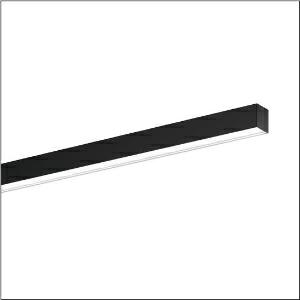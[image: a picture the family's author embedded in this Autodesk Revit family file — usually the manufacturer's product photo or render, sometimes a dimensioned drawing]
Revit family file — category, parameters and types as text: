
# Revit family: silica_r__21_51mx23tbt5b_7df7
name_source: partatom
category: Lighting Fixtures
units: mm (PartAtom-declared; Revit-internal decimal feet)

## family parameters
Cut with Voids When Loaded = No
Host = Face
Light Source = No
Part Type = Normal
Room Calculation Point = No
Round Connector Dimension = Use Diameter
Shared = No

## types (1)
- --- (1 x LED, 4030 lm, 40.5 W, 6500K)
    Apparent Load = 41 VA
    CIE Flux Codes = 78 96 99 100 100
    Color Rendering = 80
    Color Temperature = 6500K
    Default Elevation = 1800 mm
    Description = Silica® 21, office luminaire, primary optical cover: prismatic diffuser, of PMMA, CAT 2 (L<= 3000cd/m²), light emission: direct distribution, primary light characteristic: symmetric, installation type: surface-mounted, LED, rated luminous flux: 4.030lm, luminous efficacy: 95lm/W, light colour: 8tw, colour temperature: 2700..6500K, control gear: ECG DALI, with terminal, 3+2-pole, max. 2.5mm², mains connection: 220..240V, AC, 50/60Hz, rated input power: 42.6W, luminaire housing, of aluminium, jet black (RAL 9005), length: 1.504mm, width: 53mm, height: 53mm, protection rating (complete): IP20, insulation class (complete): insulation class I (protective earthing), certification: CE, permissible operating ambient temperature: 0..+35°C, standard: EN 50419, packaging unit: 1 piece
    Height = 0 mm  [stored 0 ft]
    Lamp = 1 x LED
    Lamp Light Flux = 4030 lm
    Lamp Power = 40.5 W
    Lamp count = 1
    Length = 1504 mm
    Luminous efficacy = 100 lm/W
    Manufacturer = Siteco
    ModVariant = No
    Model = 51MX23TBT5B
    Mounting Place = Ceiling
    Mounting Type = Recessed
    Number of Poles = 1
    OnlyDefault = Yes
    Power Factor = 1
    Product Name = Silica® 21
    Product group = office luminaire | ceiling recessed
    ProductGroupID = 400
    Protection Class = Protection class I
    Protection Degree = IP 20
    RLX_Detail_Level = 1
    RLX_Emergency_Light_Flux = 0 lm
    RLX_Emergency_Type = 0
    RLX_Emergency_Type_DB = No
    RlxData = <blob elided: 20473 chars, md5=a72c3dd7>
    Socket = socket
    Standby Power = 0 W
    System Light Flux = 4030 lm
    System Power = 41 W
    Type Comments = individual setting
    Type Image = l_1335925.jpg
    URL = http://relux.com
    VarID = @adj_109615
    Voltage = 0 V
    Weight = 0.00 kg
    Width = 53 mm

note: [stored X ft] marks values corroborated as IEEE doubles in the binary element streams (Revit-internal decimal feet)

## geometry (parser evidence)
native form markers: Blend x4, Sweep x11
no freeform markers — native parametric forms only
